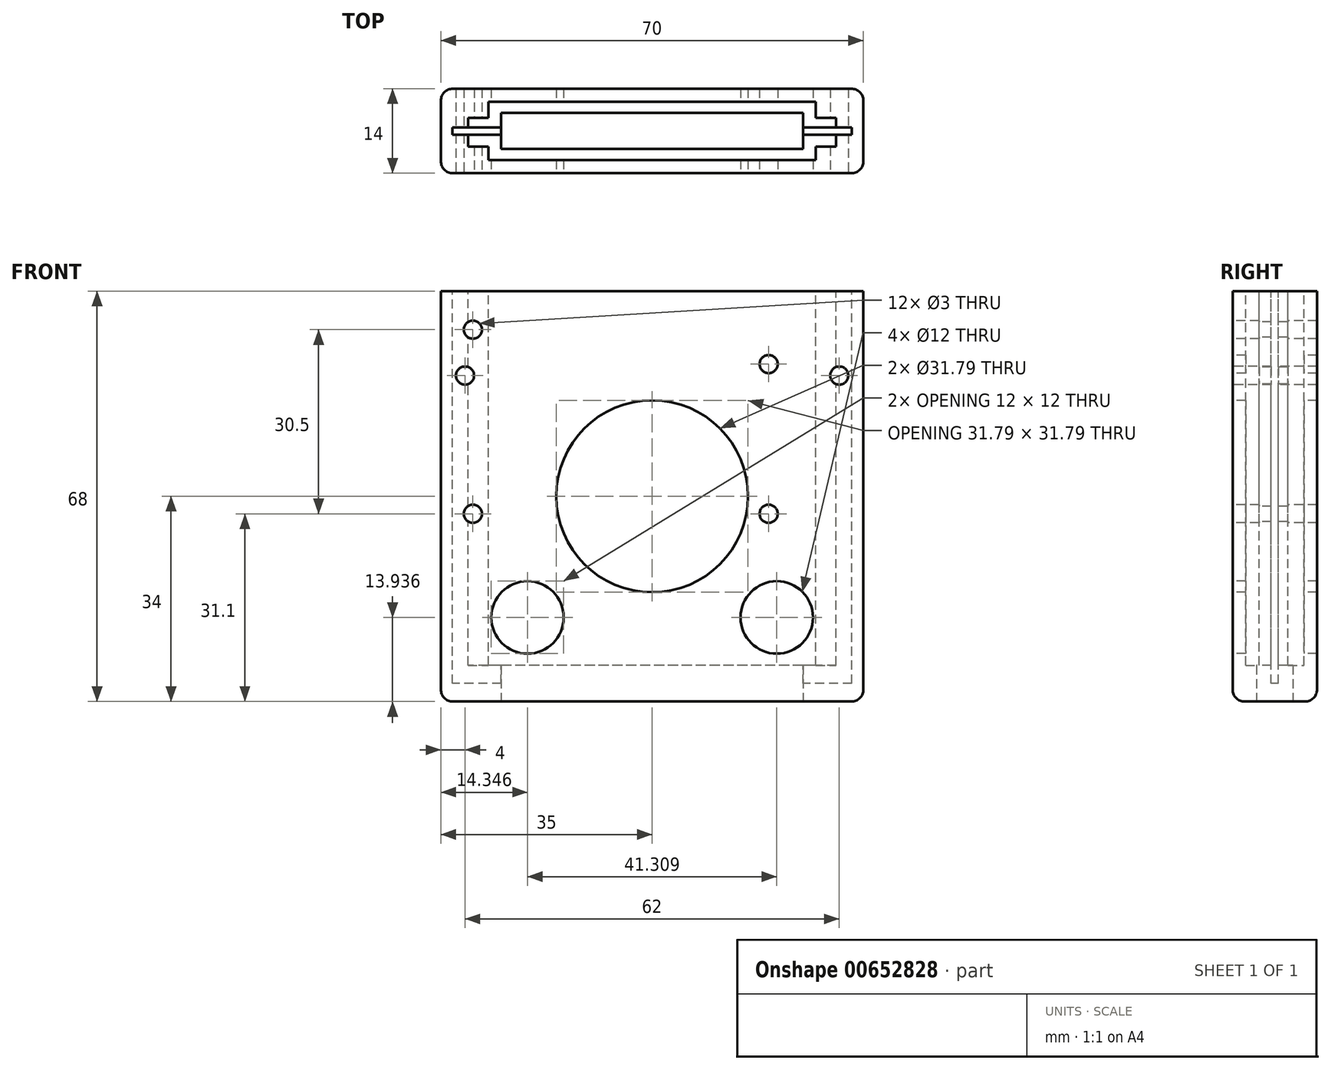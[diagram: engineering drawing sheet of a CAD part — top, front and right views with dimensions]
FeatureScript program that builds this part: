
annotation { "Feature Type Name" : "Feature", "Feature Type Description" : "" }
export const myFeature = defineFeature(function(context is Context, id is Id, definition is map)
    precondition{}
    {
        {
            var Q0;
            Q0=qCreatedBy(makeId("Top.planeOp"),FACE);
            var sketch = newSketch(context, id + "F0", { "sketchPlane" : qUnion([Q0])});
            skLineSegment(sketch, "E0.bottom", {"start": v(0, 0) * mm, "end": v(70, 0) * mm});
            skLineSegment(sketch, "E0.top", {"start": v(0, 14) * mm, "end": v(70, 14) * mm});
            skLineSegment(sketch, "E0.left", {"start": v(0, 0) * mm, "end": v(0, 14) * mm});
            skLineSegment(sketch, "E0.right", {"start": v(70, 0) * mm, "end": v(70, 14) * mm});
            skSolve(sketch);
        }
        {
            var Q0;
            Q0=makeQuery(id+"F0.imprint","IMPRINT",FACE,{"disambiguationData":[TD([[makeQuery(id+"F0.imprint","IMPRINT",EDGE,{"derivedFrom":sQuery(id+"F0.wireOp",EDGE,"E0.bottom")}),1.0]])]});
            extrude(context, id + "F1", {"entities" : qUnion([Q0]), "depth" : 68 * mm, "offsetDistance" : 25 * mm});
        }
        {
            var Q0;
            Q0=makeQuery(id+"F1.opExtrude","CAP_FACE",FACE,{"disambiguationData":[OSD([sQuery(id+"F0.wireOp",EDGE,"E0.bottom"),sQuery(id+"F0.wireOp",EDGE,"E0.top"),sQuery(id+"F0.wireOp",EDGE,"E0.left"),sQuery(id+"F0.wireOp",EDGE,"E0.right")])],"isStart":false});
            var sketch = newSketch(context, id + "F2", { "sketchPlane" : qUnion([Q0])});
            skLineSegment(sketch, "E1.bottom", {"start": v(68.1, 6.4) * mm, "end": v(1.9, 6.4) * mm});
            skLineSegment(sketch, "E1.top", {"start": v(68.1, 7.6) * mm, "end": v(1.9, 7.6) * mm});
            skLineSegment(sketch, "E1.left", {"start": v(68.1, 6.4) * mm, "end": v(68.1, 7.6) * mm});
            skLineSegment(sketch, "E1.right", {"start": v(1.9, 6.4) * mm, "end": v(1.9, 7.6) * mm});
            skPoint(sketch, "E1.middle", {"position": v(35, 7) * mm});
            skLineSegment(sketch, "E2.bottom", {"start": v(62.1, 11.82) * mm, "end": v(7.9, 11.82) * mm});
            skLineSegment(sketch, "E2.top", {"start": v(62.1, 2.18) * mm, "end": v(7.9, 2.18) * mm});
            skLineSegment(sketch, "E2.left", {"start": v(65.5, 9.2) * mm, "end": v(65.5, 7.6) * mm});
            skLineSegment(sketch, "E2.right", {"start": v(4.5, 9.2) * mm, "end": v(4.5, 7.6) * mm});
            skPoint(sketch, "E3.orphan", {"position": v(0, 7) * mm});
            skPoint(sketch, "E4.end.orphan", {"position": v(70, 7) * mm});
            skLineSegment(sketch, "E5.trimOffspring", {"start": v(65.5, 6.4) * mm, "end": v(65.5, 4.3) * mm});
            skLineSegment(sketch, "E6.trimOffspring", {"start": v(4.5, 6.4) * mm, "end": v(4.5, 4.4) * mm});
            skLineSegment(sketch, "E7.left", {"start": v(62.1, 2.18) * mm, "end": v(62.1, 4.4) * mm});
            skLineSegment(sketch, "E7.right", {"start": v(7.9, 2.18) * mm, "end": v(7.9, 4.4) * mm});
            skLineSegment(sketch, "E8", {"start": v(4.5, 9.2) * mm, "end": v(7.9, 9.2) * mm});
            skLineSegment(sketch, "E9", {"start": v(62.1, 9.2) * mm, "end": v(65.5, 9.2) * mm});
            skLineSegment(sketch, "E10", {"start": v(4.5, 4.4) * mm, "end": v(7.9, 4.4) * mm});
            skLineSegment(sketch, "E11", {"start": v(62.1, 4.4) * mm, "end": v(65.5, 4.4) * mm});
            skPoint(sketch, "E11.endSnap0", {"position": v(65.5, 4.3) * mm});
            skLineSegment(sketch, "E12.trimOffspring", {"start": v(7.9, 9.2) * mm, "end": v(7.9, 11.82) * mm});
            skLineSegment(sketch, "E13.trimOffspring", {"start": v(62.1, 9.2) * mm, "end": v(62.1, 11.82) * mm});
            skPoint(sketch, "E14.orphan", {"position": v(65.5, 2.18) * mm});
            skPoint(sketch, "E15.orphan", {"position": v(65.5, 11.82) * mm});
            skPoint(sketch, "E16.orphan", {"position": v(4.5, 11.82) * mm});
            skPoint(sketch, "E17.orphan", {"position": v(4.5, 2.18) * mm});
            skSolve(sketch);
        }
        {
            var Q0;
            Q0=makeQuery(id+"F1.opExtrude","SWEPT_FACE",FACE,{"disambiguationData":[OSD([sQuery(id+"F0.wireOp",EDGE,"E0.bottom")])]});
            var sketch = newSketch(context, id + "F3", { "sketchPlane" : qUnion([Q0])});
            skCircle(sketch, "E18", {"center": v(5.3, 61.6) * mm, "radius": 1.5 * mm});
            skCircle(sketch, "E19", {"center": v(54.3, 55.9) * mm, "radius": 1.5 * mm});
            skCircle(sketch, "E20", {"center": v(54.3, 31.1) * mm, "radius": 1.5 * mm});
            skCircle(sketch, "E21", {"center": v(5.3, 31.1) * mm, "radius": 1.5 * mm});
            skPoint(sketch, "E22.orphan", {"position": v(35, 68) * mm});
            skLineSegment(sketch, "E23", {"start": v(0, 54) * mm, "end": v(2.5, 54) * mm});
            skPoint(sketch, "E24.start.orphan", {"position": v(-8.16, 54) * mm});
            skPoint(sketch, "E25.start.orphan", {"position": v(66, 72.3) * mm});
            skCircle(sketch, "E26", {"center": v(66, 54) * mm, "radius": 1.5 * mm});
            skCircle(sketch, "E27", {"center": v(4, 54) * mm, "radius": 1.5 * mm});
            skPoint(sketch, "E28.start.orphan", {"position": v(66, 68) * mm});
            skCircle(sketch, "E29", {"center": v(35, 34) * mm, "radius": 15.9 * mm});
            skCircle(sketch, "E30", {"center": v(55.65, 13.94) * mm, "radius": 6 * mm});
            skCircle(sketch, "E31", {"center": v(14.35, 13.94) * mm, "radius": 6 * mm});
            skSolve(sketch);
        }
        {
            var Q0;
            Q0=makeQuery(id+"F3.imprint","IMPRINT",FACE,{"disambiguationData":[TD([[makeQuery(id+"F3.imprint","IMPRINT",EDGE,{"derivedFrom":sQuery(id+"F3.wireOp",EDGE,"E18")}),1.0]])]});
            var Q1;
            Q1=makeQuery(id+"F3.imprint","IMPRINT",FACE,{"disambiguationData":[TD([[makeQuery(id+"F3.imprint","IMPRINT",EDGE,{"derivedFrom":sQuery(id+"F3.wireOp",EDGE,"E27")}),1.0]])]});
            var Q2;
            Q2=makeQuery(id+"F3.imprint","IMPRINT",FACE,{"disambiguationData":[TD([[makeQuery(id+"F3.imprint","IMPRINT",EDGE,{"derivedFrom":sQuery(id+"F3.wireOp",EDGE,"E21")}),1.0]])]});
            var Q3;
            Q3=makeQuery(id+"F3.imprint","IMPRINT",FACE,{"disambiguationData":[TD([[makeQuery(id+"F3.imprint","IMPRINT",EDGE,{"derivedFrom":sQuery(id+"F3.wireOp",EDGE,"E20")}),1.0]])]});
            var Q4;
            Q4=makeQuery(id+"F3.imprint","IMPRINT",FACE,{"disambiguationData":[TD([[makeQuery(id+"F3.imprint","IMPRINT",EDGE,{"derivedFrom":sQuery(id+"F3.wireOp",EDGE,"E19")}),1.0]])]});
            var Q5;
            Q5=makeQuery(id+"F3.imprint","IMPRINT",FACE,{"disambiguationData":[TD([[makeQuery(id+"F3.imprint","IMPRINT",EDGE,{"derivedFrom":sQuery(id+"F3.wireOp",EDGE,"E26")}),1.0]])]});
            var Q6;
            Q6=makeQuery(id+"F3.imprint","IMPRINT",FACE,{"disambiguationData":[TD([[makeQuery(id+"F3.imprint","IMPRINT",EDGE,{"derivedFrom":sQuery(id+"F3.wireOp",EDGE,"E29")}),1.0]])]});
            var Q7;
            Q7=makeQuery(id+"F3.imprint","IMPRINT",FACE,{"disambiguationData":[TD([[makeQuery(id+"F3.imprint","IMPRINT",EDGE,{"derivedFrom":sQuery(id+"F3.wireOp",EDGE,"E31")}),1.0]])]});
            var Q8;
            Q8=makeQuery(id+"F3.imprint","IMPRINT",FACE,{"disambiguationData":[TD([[makeQuery(id+"F3.imprint","IMPRINT",EDGE,{"derivedFrom":sQuery(id+"F3.wireOp",EDGE,"E30")}),1.0]])]});
            extrude(context, id + "F4", {"entities" : qUnion([Q0, Q1, Q2, Q3, Q4, Q5, Q6, Q7, Q8]), "operationType" : NewBodyOperationType.REMOVE, "oppositeDirection" : true, "depth" : 14 * mm, "offsetDistance" : 25 * mm});
        }
        {
            var Q0;
            {var subQ0=sQuery(id+"F2.wireOp",EDGE,"E1.left");Q0=makeQuery(id+"F2.imprint","IMPRINT",FACE,{"disambiguationData":[TD([[makeQuery(id+"F2.imprint","IMPRINT",EDGE,{"derivedFrom":subQ0}),1.0]])]});}
            extrude(context, id + "F5", {"entities" : qUnion([Q0]), "operationType" : NewBodyOperationType.REMOVE, "oppositeDirection" : true, "depth" : 65 * mm, "offsetDistance" : 25 * mm});
        }
        {
            var Q0;
            {var subQ0=sQuery(id+"F2.wireOp",EDGE,"E2.left");Q0=makeQuery(id+"F2.imprint","IMPRINT",FACE,{"disambiguationData":[TD([[makeQuery(id+"F2.imprint","IMPRINT",EDGE,{"derivedFrom":subQ0}),-1.0]])]});}
            var Q1;
            {var subQ3=sQuery(id+"F2.wireOp",EDGE,"E6.trimOffspring");Q1=makeQuery(id+"F2.imprint","IMPRINT",FACE,{"disambiguationData":[TD([[makeQuery(id+"F2.imprint","IMPRINT",EDGE,{"derivedFrom":subQ3}),1.0]])]});}
            extrude(context, id + "F6", {"entities" : qUnion([Q0, Q1]), "operationType" : NewBodyOperationType.REMOVE, "oppositeDirection" : true, "depth" : 62 * mm, "offsetDistance" : 25 * mm});
        }
        {
            var Q0;
            Q0=makeQuery(id+"F1.opExtrude","SWEPT_EDGE",EDGE,{"disambiguationData":[OSD([sQuery(id+"F0.wireOp",EDGE,"E0.bottom"),sQuery(id+"F0.wireOp",EDGE,"E0.left")])]});
            var Q1;
            Q1=makeQuery(id+"F1.opExtrude","SWEPT_EDGE",EDGE,{"disambiguationData":[OSD([sQuery(id+"F0.wireOp",EDGE,"E0.top"),sQuery(id+"F0.wireOp",EDGE,"E0.left")])]});
            var Q2;
            Q2=makeQuery(id+"F1.opExtrude","SWEPT_EDGE",EDGE,{"disambiguationData":[OSD([sQuery(id+"F0.wireOp",EDGE,"E0.bottom"),sQuery(id+"F0.wireOp",EDGE,"E0.right")])]});
            var Q3;
            Q3=makeQuery(id+"F1.opExtrude","SWEPT_EDGE",EDGE,{"disambiguationData":[OSD([sQuery(id+"F0.wireOp",EDGE,"E0.top"),sQuery(id+"F0.wireOp",EDGE,"E0.right")])]});
            var Q4;
            Q4=makeQuery(id+"F1.opExtrude","CAP_EDGE",EDGE,{"disambiguationData":[OSD([sQuery(id+"F0.wireOp",EDGE,"E0.bottom")])],"isStart":true});
            var Q5;
            Q5=makeQuery(id+"F1.opExtrude","CAP_EDGE",EDGE,{"disambiguationData":[OSD([sQuery(id+"F0.wireOp",EDGE,"E0.top")])],"isStart":true});
            var Q6;
            Q6=makeQuery(id+"F1.opExtrude","CAP_EDGE",EDGE,{"disambiguationData":[OSD([sQuery(id+"F0.wireOp",EDGE,"E0.left")])],"isStart":true});
            var Q7;
            Q7=makeQuery(id+"F1.opExtrude","CAP_EDGE",EDGE,{"disambiguationData":[OSD([sQuery(id+"F0.wireOp",EDGE,"E0.right")])],"isStart":true});
            fillet(context, id + "F7", {"entities" : qUnion([Q0, Q1, Q2, Q3, Q4, Q5, Q6, Q7]), "radius" : 2 * mm, "tangentPropagation" : true, "allowEdgeOverflow" : false});
        }
        {
            var Q0;
            Q0=makeQuery(id+"F1.opExtrude","CAP_FACE",FACE,{"disambiguationData":[OSD([sQuery(id+"F0.wireOp",EDGE,"E0.bottom"),sQuery(id+"F0.wireOp",EDGE,"E0.top"),sQuery(id+"F0.wireOp",EDGE,"E0.left"),sQuery(id+"F0.wireOp",EDGE,"E0.right")])],"isStart":true});
            var sketch = newSketch(context, id + "F8", { "sketchPlane" : qUnion([Q0])});
            skLineSegment(sketch, "E32.bottom", {"start": v(10, -4) * mm, "end": v(60, -4) * mm});
            skLineSegment(sketch, "E32.top", {"start": v(10, -10) * mm, "end": v(60, -10) * mm});
            skLineSegment(sketch, "E32.left", {"start": v(10, -4) * mm, "end": v(10, -10) * mm});
            skLineSegment(sketch, "E32.right", {"start": v(60, -4) * mm, "end": v(60, -10) * mm});
            skPoint(sketch, "E32.middle", {"position": v(35, -7) * mm});
            skPoint(sketch, "E33.trimOffspring.end.orphan", {"position": v(35, -2) * mm});
            skPoint(sketch, "E34.start.orphan", {"position": v(35, -12) * mm});
            skSolve(sketch);
        }
        {
            var Q0;
            Q0=makeQuery(id+"F8.imprint","IMPRINT",FACE,{"disambiguationData":[TD([[makeQuery(id+"F8.imprint","IMPRINT",EDGE,{"derivedFrom":sQuery(id+"F8.wireOp",EDGE,"E32.bottom")}),-1.0]])]});
            extrude(context, id + "F9", {"entities" : qUnion([Q0]), "operationType" : NewBodyOperationType.REMOVE, "oppositeDirection" : true, "depth" : 10 * mm, "offsetDistance" : 25 * mm});
        }
    });
